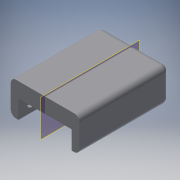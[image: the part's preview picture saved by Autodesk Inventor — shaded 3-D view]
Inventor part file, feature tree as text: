
AUTODESK INVENTOR PART (.ipt)
format: ipt  version: 2018 (Build 220112000, 112)  size: 203,776 bytes
history: native  units: mm
features: extrude x5, sketch x5, reference x5, plane x3, other x3, fillet x2, mirror x1
ambient origin geometry x8: Origin, YZ Plane, XZ Plane, XY Plane, X Axis, Y Axis, Z Axis, Center Point
bodies: Solid1 (feature_tree)
feature tree (24):
  extrude  "Extrusion1"  Depth=3.0mm
  extrude  "Extrusion2"  Depth=2.0mm TaperAngle=0.0deg
  sketch  "Sketch3"  dims[d5=5.0mm d6=5.0mm]
  plane  "Work Plane1"
  extrude  "Extrusion3"  Depth=5.0mm
  extrude  "Extrusion4"  Depth=2.0mm TaperAngle=0.0deg
  plane  "Work Plane2"
  mirror  "Mirror1"
  fillet  "Fillet1"  Radius=2.9mm
  fillet  "Fillet2"  Radius=2.9mm
  extrude  "Extrusion5"  Depth=2.0mm TaperAngle=0.0deg
  sketch  "Sketch1"  dims[d0=3.0mm d1=3.0mm]
  reference  "Reference1"
  reference  "Reference2"
  reference  "Reference3"
  reference  "Reference4"
  sketch  "Sketch2"  dims[d2=3.0mm d3=2.0mm d4=0.0mm]
  sketch  "Sketch4"  dims[d7=4.0mm d8=2.0mm d9=0.0mm d10=2.9mm d11=2.9mm]
  reference  "Reference5"
  plane  "Work Plane3"
  sketch  "Sketch5"  dims[d12=2.9mm d13=2.0mm d14=0.0mm d15=0.3mm d16=0.3mm d17=1.3mm d18=0.0mm d19=2.0mm d20=2.0mm d21=4.0mm d22=1.7mm d23=0.0mm]
  other  "<userpath>\Dropbox\Skola\Projekt\Kretsn_Brillz_V2\3D\Programmer_mini\Programmer_mini.iam"
  other  "Programmer_mini.iam"
  other  "Top:1"
